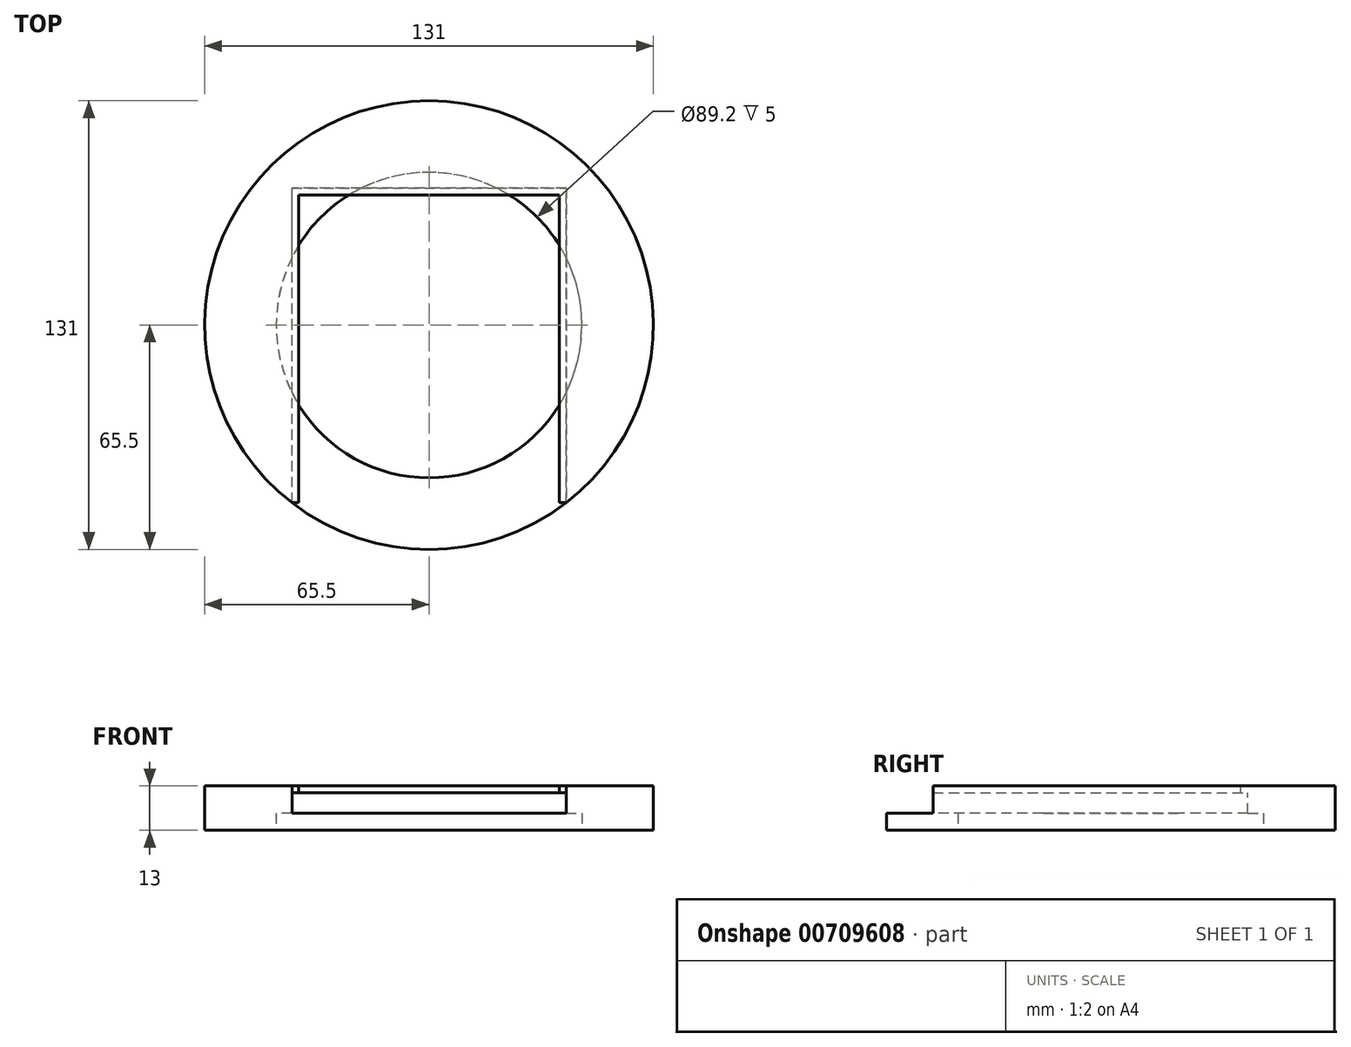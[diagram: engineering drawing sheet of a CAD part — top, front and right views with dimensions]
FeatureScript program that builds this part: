
annotation { "Feature Type Name" : "Feature", "Feature Type Description" : "" }
export const myFeature = defineFeature(function(context is Context, id is Id, definition is map)
    precondition{}
    {
        {
            var Q0;
            Q0=qCreatedBy(makeId("Top.planeOp"),FACE);
            var sketch = newSketch(context, id + "F0", { "sketchPlane" : qUnion([Q0])});
            skCircle(sketch, "E0", {"center": v(0, 0) * mm, "radius": 65.5 * mm});
            skSolve(sketch);
        }
        {
            var Q0;
            Q0 = qSketchRegion(id + "F0", true);
            extrude(context, id + "F1", {"entities" : qUnion([Q0]), "depth" : 13 * mm, "offsetDistance" : 25 * mm});
        }
        {
            var Q0;
            Q0=qCreatedBy(makeId("Top.planeOp"),FACE);
            var sketch = newSketch(context, id + "F2", { "sketchPlane" : qUnion([Q0])});
            skCircle(sketch, "E1", {"center": v(0, 0) * mm, "radius": 44.6 * mm});
            skCircle(sketch, "E2.0", {"center": v(0, 0) * mm, "radius": 70.5 * mm});
            skCircle(sketch, "E3.0", {"center": v(0, 0) * mm, "radius": 34.6 * mm});
            skSolve(sketch);
        }
        {
            var Q0;
            Q0=makeQuery(id+"F2.imprint","IMPRINT",FACE,{"disambiguationData":[TD([[makeQuery(id+"F2.imprint","IMPRINT",EDGE,{"derivedFrom":sQuery(id+"F2.wireOp",EDGE,"E3.0")}),1.0]])]});
            var Q1;
            Q1=makeQuery(id+"F2.imprint","IMPRINT",FACE,{"disambiguationData":[TD([[makeQuery(id+"F2.imprint","IMPRINT",EDGE,{"derivedFrom":sQuery(id+"F2.wireOp",EDGE,"E1")}),1.0]])]});
            extrude(context, id + "F3", {"entities" : qUnion([Q0, Q1]), "operationType" : NewBodyOperationType.REMOVE, "depth" : 5 * mm, "offsetDistance" : 25 * mm});
        }
        {
            var Q0;
            Q0=makeQuery(id+"F1.opExtrude","CAP_FACE",FACE,{"disambiguationData":[OSD([sQuery(id+"F0.wireOp",EDGE,"E0")])],"isStart":true});
            var sketch = newSketch(context, id + "F4", { "sketchPlane" : qUnion([Q0])});
            skCircle(sketch, "E4.0", {"center": v(0, 0) * mm, "radius": 34.6 * mm});
            skCircle(sketch, "E5.0", {"center": v(0, 0) * mm, "radius": 39.6 * mm});
            skSolve(sketch);
        }
        {
            var Q0;
            Q0=makeQuery(id+"F4.imprint","IMPRINT",FACE,{"disambiguationData":[TD([[makeQuery(id+"F4.imprint","IMPRINT",EDGE,{"derivedFrom":sQuery(id+"F4.wireOp",EDGE,"E4.0")}),1.0]])]});
            extrude(context, id + "F5", {"entities" : qUnion([Q0]), "operationType" : NewBodyOperationType.REMOVE, "oppositeDirection" : true, "depth" : 25 * mm, "offsetDistance" : 25 * mm});
        }
        {
            var Q0;
            Q0=makeQuery(id+"F1.opExtrude","CAP_FACE",FACE,{"disambiguationData":[OSD([sQuery(id+"F0.wireOp",EDGE,"E0")])],"isStart":false});
            var sketch = newSketch(context, id + "F6", { "sketchPlane" : qUnion([Q0])});
            skLineSegment(sketch, "E6", {"start": v(0, 0) * mm, "end": v(40, 0) * mm});
            skLineSegment(sketch, "E7", {"start": v(40, 0) * mm, "end": v(40, -74.89) * mm});
            skLineSegment(sketch, "E8", {"start": v(40, -74.89) * mm, "end": v(0, -74.89) * mm});
            skLineSegment(sketch, "E9", {"start": v(0, -74.89) * mm, "end": v(-40, -74.89) * mm});
            skLineSegment(sketch, "E10", {"start": v(-40, -74.89) * mm, "end": v(-40, 0) * mm});
            skLineSegment(sketch, "E11", {"start": v(-40, 0) * mm, "end": v(0, 0) * mm});
            skLineSegment(sketch, "E12", {"start": v(-40, 0) * mm, "end": v(-40, 40) * mm});
            skLineSegment(sketch, "E13", {"start": v(-40, 40) * mm, "end": v(40, 40) * mm});
            skLineSegment(sketch, "E14", {"start": v(40, 40) * mm, "end": v(40, 0) * mm});
            skSolve(sketch);
        }
        {
            var Q0;
            {var subQ0=sQuery(id+"F6.wireOp",EDGE,"E12");Q0=makeQuery(id+"F6.imprint","IMPRINT",FACE,{"disambiguationData":[TD([[makeQuery(id+"F6.imprint","IMPRINT",EDGE,{"derivedFrom":subQ0}),-1.0]])]});}
            var Q1;
            {var subQ3=sQuery(id+"F0.wireOp",EDGE,"E0");var subQ6=makeQuery(id+"F1.opExtrude","CAP_EDGE",EDGE,{"disambiguationData":[OSD([subQ3])],"isStart":false});var subQ8=sQuery(id+"F6.wireOp",EDGE,"E7");var subQ11=makeQuery(id+"F6.imprint","INTERSECT",VERTEX,{"derivedFrom":[subQ6,subQ8]});Q1=makeQuery(id+"F6.imprint","IMPRINT",FACE,{"disambiguationData":[TD([[makeQuery(id+"F6.imprint","IMPRINT",EDGE,{"disambiguationData":[TD([[subQ11,1.0]])],"derivedFrom":subQ6}),1.0]])]});}
            extrude(context, id + "F7", {"entities" : qUnion([Q0, Q1]), "operationType" : NewBodyOperationType.REMOVE, "oppositeDirection" : true, "depth" : 8 * mm, "offsetDistance" : 25 * mm});
        }
        {
            var Q0;
            Q0=makeQuery(id+"F7.boolean.opBoolean","COPY",FACE,{"derivedFrom":makeQuery(id+"F7.opExtrude","SWEPT_FACE",FACE,{"disambiguationData":[OSD([sQuery(id+"F6.wireOp",EDGE,"E10"),sQuery(id+"F6.wireOp",EDGE,"E12")])]})});
            var sketch = newSketch(context, id + "F8", { "sketchPlane" : qUnion([Q0])});
            skLineSegment(sketch, "E15", {"start": v(-48.34, 13) * mm, "end": v(-48.34, 11) * mm});
            skLineSegment(sketch, "E16", {"start": v(-48.34, 11) * mm, "end": v(40, 11) * mm});
            skLineSegment(sketch, "E17", {"start": v(40, 11) * mm, "end": v(40, 13) * mm});
            skLineSegment(sketch, "E18", {"start": v(40, 13) * mm, "end": v(-48.34, 13) * mm});
            skLineSegment(sketch, "E19", {"start": v(-48.34, 11) * mm, "end": v(-51.87, 11) * mm});
            skLineSegment(sketch, "E20", {"start": v(-51.87, 11) * mm, "end": v(-51.87, 13) * mm});
            skLineSegment(sketch, "E21", {"start": v(-51.87, 13) * mm, "end": v(-48.34, 13) * mm});
            skSolve(sketch);
        }
        {
            var Q0;
            Q0=makeQuery(id+"F8.imprint","IMPRINT",FACE,{"disambiguationData":[TD([[makeQuery(id+"F8.imprint","IMPRINT",EDGE,{"derivedFrom":sQuery(id+"F8.wireOp",EDGE,"E15")}),1.0]])]});
            extrude(context, id + "F9", {"entities" : qUnion([Q0]), "operationType" : NewBodyOperationType.ADD, "depth" : 2 * mm, "offsetDistance" : 25 * mm});
        }
        {
            var Q0;
            Q0=makeQuery(id+"F7.boolean.opBoolean","COPY",FACE,{"derivedFrom":makeQuery(id+"F7.opExtrude","SWEPT_FACE",FACE,{"disambiguationData":[OSD([sQuery(id+"F6.wireOp",EDGE,"E13")])]})});
            var sketch = newSketch(context, id + "F10", { "sketchPlane" : qUnion([Q0])});
            skLineSegment(sketch, "E22", {"start": v(-38, 11) * mm, "end": v(40, 11) * mm});
            skLineSegment(sketch, "E23", {"start": v(40, 11) * mm, "end": v(40, 13) * mm});
            skLineSegment(sketch, "E24", {"start": v(40, 13) * mm, "end": v(-38, 13) * mm});
            skLineSegment(sketch, "E25", {"start": v(-38, 13) * mm, "end": v(-38, 11) * mm});
            skSolve(sketch);
        }
        {
            var Q0;
            Q0 = qSketchRegion(id + "F10", true);
            extrude(context, id + "F11", {"entities" : qUnion([Q0]), "operationType" : NewBodyOperationType.ADD, "depth" : 2 * mm, "offsetDistance" : 25 * mm});
        }
        {
            var Q0;
            Q0=makeQuery(id+"F7.boolean.opBoolean","COPY",FACE,{"derivedFrom":makeQuery(id+"F7.opExtrude","SWEPT_FACE",FACE,{"disambiguationData":[OSD([sQuery(id+"F6.wireOp",EDGE,"E7"),sQuery(id+"F6.wireOp",EDGE,"E14")])]})});
            var sketch = newSketch(context, id + "F12", { "sketchPlane" : qUnion([Q0])});
            skLineSegment(sketch, "E26", {"start": v(-38, 11) * mm, "end": v(51.87, 11) * mm});
            skLineSegment(sketch, "E27", {"start": v(51.87, 11) * mm, "end": v(51.87, 13) * mm});
            skLineSegment(sketch, "E28", {"start": v(51.87, 13) * mm, "end": v(-38, 13) * mm});
            skLineSegment(sketch, "E29", {"start": v(-38, 13) * mm, "end": v(-38, 11) * mm});
            skSolve(sketch);
        }
        {
            var Q0;
            Q0 = qSketchRegion(id + "F12", true);
            extrude(context, id + "F13", {"entities" : qUnion([Q0]), "operationType" : NewBodyOperationType.ADD, "depth" : 2 * mm, "offsetDistance" : 25 * mm});
        }
        {
            var Q0;
            Q0 = qSketchRegion(id + "F8", true);
            extrude(context, id + "F14", {"entities" : qUnion([Q0]), "operationType" : NewBodyOperationType.ADD, "depth" : 2 * mm, "offsetDistance" : 25 * mm});
        }
    });
